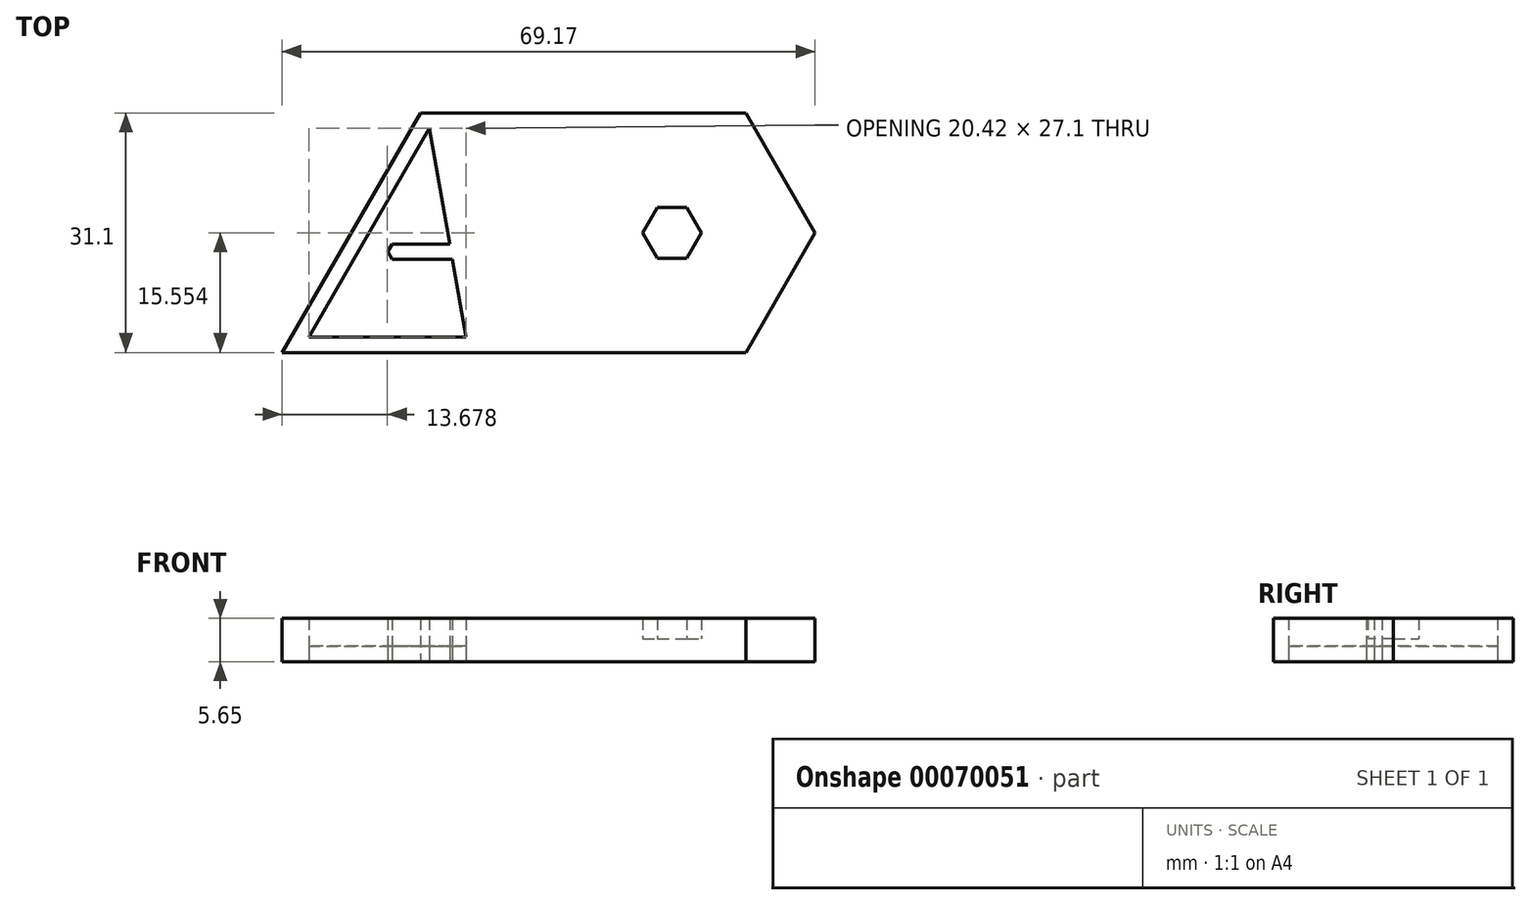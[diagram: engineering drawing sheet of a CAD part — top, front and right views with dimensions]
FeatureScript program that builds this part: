
annotation { "Feature Type Name" : "Feature", "Feature Type Description" : "" }
export const myFeature = defineFeature(function(context is Context, id is Id, definition is map)
    precondition{}
    {
        {
            var Q0;
            Q0=qCreatedBy(makeId("Top.planeOp"),FACE);
            var sketch = newSketch(context, id + "F0", { "sketchPlane" : qUnion([Q0])});
            skLineSegment(sketch, "E0", {"start": v(-58.85, -4.43) * mm, "end": v(-38.43, -4.43) * mm});
            skLineSegment(sketch, "E1", {"start": v(-38.43, -4.43) * mm, "end": v(-43.2, 22.67) * mm});
            skLineSegment(sketch, "E2", {"start": v(-43.2, 22.67) * mm, "end": v(-58.85, -4.43) * mm});
            skLineSegment(sketch, "E3", {"start": v(-40.2, 5.66) * mm, "end": v(-48, 5.66) * mm});
            skLineSegment(sketch, "E4", {"start": v(-38.43, -4.43) * mm, "end": v(-3.28, -4.43) * mm});
            skLineSegment(sketch, "E5", {"start": v(-43.2, 22.67) * mm, "end": v(-3.28, 22.67) * mm});
            skLineSegment(sketch, "E6", {"start": v(-3.28, -4.43) * mm, "end": v(4.54, 9.12) * mm});
            skLineSegment(sketch, "E7", {"start": v(4.54, 9.12) * mm, "end": v(-3.28, 22.67) * mm});
            skPoint(sketch, "E8.endSnap0", {"position": v(-40.82, 9.12) * mm});
            skLineSegment(sketch, "E9.0", {"start": v(-44.36, 24.67) * mm, "end": v(-2.86, 24.67) * mm});
            skLineSegment(sketch, "E9.1", {"start": v(-62.32, -6.43) * mm, "end": v(-38.92, -6.43) * mm});
            skLineSegment(sketch, "E9.2", {"start": v(-38.92, -6.43) * mm, "end": v(-2.13, -6.43) * mm});
            skLineSegment(sketch, "E9.3", {"start": v(-44.36, 24.67) * mm, "end": v(-62.32, -6.43) * mm});
            skLineSegment(sketch, "E9.4", {"start": v(-2.13, -6.43) * mm, "end": v(6.85, 9.12) * mm});
            skLineSegment(sketch, "E10", {"start": v(-48, 7.66) * mm, "end": v(-40.56, 7.66) * mm});
            skLineSegment(sketch, "E11", {"start": v(-41.2, 22.67) * mm, "end": v(-36.43, -4.43) * mm});
            skLineSegment(sketch, "E12", {"start": v(-43.2, 22.67) * mm, "end": v(-41.2, 22.67) * mm});
            skLineSegment(sketch, "E13", {"start": v(-23.52, -4.43) * mm, "end": v(-25.52, -4.43) * mm});
            skLineSegment(sketch, "E14", {"start": v(-33.49, 8.88) * mm, "end": v(-25.52, 8.88) * mm});
            skLineSegment(sketch, "E15", {"start": v(-22.8, 10.88) * mm, "end": v(-33.49, 10.88) * mm});
            skLineSegment(sketch, "E16", {"start": v(-25.6, 14.8) * mm, "end": v(-33.29, 22.67) * mm});
            skLineSegment(sketch, "E17", {"start": v(-48, 5.66) * mm, "end": v(-48.59, 6.66) * mm});
            skLineSegment(sketch, "E18", {"start": v(-48.59, 6.66) * mm, "end": v(-48, 7.66) * mm});
            skLineSegment(sketch, "E19", {"start": v(-33.49, 8.88) * mm, "end": v(-34.07, 9.88) * mm});
            skLineSegment(sketch, "E20", {"start": v(-34.07, 9.88) * mm, "end": v(-33.49, 10.88) * mm});
            skLineSegment(sketch, "E21", {"start": v(-24.17, 16.19) * mm, "end": v(-30.54, 22.67) * mm});
            skLineSegment(sketch, "E22", {"start": v(-25.6, 14.8) * mm, "end": v(-24.48, 15.08) * mm});
            skLineSegment(sketch, "E23", {"start": v(-24.48, 15.08) * mm, "end": v(-24.17, 16.19) * mm});
            skLineSegment(sketch, "E24", {"start": v(-25.52, 8.88) * mm, "end": v(-23.18, -4.43) * mm});
            skLineSegment(sketch, "E25", {"start": v(-22.8, 10.88) * mm, "end": v(-20.1, -4.43) * mm});
            skLineSegment(sketch, "E26", {"start": v(-24.48, 15.08) * mm, "end": v(-20.1, 22.67) * mm});
            skLineSegment(sketch, "E27", {"start": v(-20.1, 22.67) * mm, "end": v(-3.28, 22.67) * mm});
            skLineSegment(sketch, "E28", {"start": v(-20.1, -4.43) * mm, "end": v(-3.28, -4.43) * mm});
            skPoint(sketch, "E29", {"position": v(-11.69, 22.67) * mm});
            skPoint(sketch, "E30", {"position": v(-11.69, 9.12) * mm});
            skCircle(sketch, "E31.cCircle", {"center": v(-11.69, 9.12) * mm, "radius": 3.3 * mm, "construction": true});
            skLineSegment(sketch, "E31.0", {"start": v(-13.6, 12.42) * mm, "end": v(-9.78, 12.42) * mm});
            skLineSegment(sketch, "E31.1", {"start": v(-9.78, 12.42) * mm, "end": v(-7.88, 9.12) * mm});
            skLineSegment(sketch, "E31.2", {"start": v(-7.88, 9.12) * mm, "end": v(-9.78, 5.82) * mm});
            skLineSegment(sketch, "E31.3", {"start": v(-9.78, 5.82) * mm, "end": v(-13.6, 5.82) * mm});
            skLineSegment(sketch, "E31.4", {"start": v(-13.6, 5.82) * mm, "end": v(-15.5, 9.12) * mm});
            skLineSegment(sketch, "E31.5", {"start": v(-15.5, 9.12) * mm, "end": v(-13.6, 12.42) * mm});
            skPoint(sketch, "E31.0.midPoint", {"position": v(-11.69, 12.42) * mm});
            skLineSegment(sketch, "E32.0", {"start": v(6.27, 10.12) * mm, "end": v(-2.13, 24.67) * mm});
            skLineSegment(sketch, "E32.1", {"start": v(-20.1, 24.67) * mm, "end": v(-2.13, 24.67) * mm});
            skLineSegment(sketch, "E33", {"start": v(6.27, 10.12) * mm, "end": v(6.85, 9.12) * mm});
            skSolve(sketch);
        }
        {
            var Q0;
            {var subQ3=sQuery(id+"F0.wireOp",EDGE,"E0");Q0=makeQuery(id+"F0.imprint","IMPRINT",FACE,{"disambiguationData":[TD([[makeQuery(id+"F0.imprint","IMPRINT",EDGE,{"derivedFrom":subQ3}),1.0]])]});}
            var Q1;
            {var subQ9=sQuery(id+"F0.wireOp",EDGE,"E6");Q1=makeQuery(id+"F0.imprint","IMPRINT",FACE,{"disambiguationData":[TD([[makeQuery(id+"F0.imprint","IMPRINT",EDGE,{"derivedFrom":subQ9}),1.0]])]});}
            extrude(context, id + "F1", {"entities" : qUnion([Q0, Q1]), "depth" : 2 * mm});
        }
        {
            var Q0;
            {var subQ3=sQuery(id+"F0.wireOp",EDGE,"E11");Q0=makeQuery(id+"F0.imprint","IMPRINT",FACE,{"disambiguationData":[TD([[makeQuery(id+"F0.imprint","IMPRINT",EDGE,{"derivedFrom":subQ3}),-1.0]])]});}
            var Q1;
            {var subQ0=sQuery(id+"F0.wireOp",EDGE,"E3");Q1=makeQuery(id+"F0.imprint","IMPRINT",FACE,{"disambiguationData":[TD([[makeQuery(id+"F0.imprint","IMPRINT",EDGE,{"derivedFrom":subQ0}),-1.0]])]});}
            var Q2;
            Q2=makeQuery(id+"F0.imprint","IMPRINT",FACE,{"disambiguationData":[TD([[makeQuery(id+"F0.imprint","IMPRINT",EDGE,{"derivedFrom":sQuery(id+"F0.wireOp",EDGE,"E14")}),1.0]])]});
            var Q3;
            {var subQ0=sQuery(id+"F0.wireOp",EDGE,"E16");Q3=makeQuery(id+"F0.imprint","IMPRINT",FACE,{"disambiguationData":[TD([[makeQuery(id+"F0.imprint","IMPRINT",EDGE,{"derivedFrom":subQ0}),-1.0]])]});}
            var Q4;
            {var subQ0=sQuery(id+"F0.wireOp",EDGE,"E21");Q4=makeQuery(id+"F0.imprint","IMPRINT",FACE,{"disambiguationData":[TD([[makeQuery(id+"F0.imprint","IMPRINT",EDGE,{"derivedFrom":subQ0}),-1.0]])]});}
            var Q5;
            {var subQ7=sQuery(id+"F0.wireOp",EDGE,"E0");Q5=makeQuery(id+"F0.imprint","IMPRINT",FACE,{"disambiguationData":[TD([[makeQuery(id+"F0.imprint","IMPRINT",EDGE,{"derivedFrom":subQ7}),-1.0]])]});}
            var Q6;
            Q6=makeQuery(id+"F0.imprint","IMPRINT",FACE,{"disambiguationData":[TD([[makeQuery(id+"F0.imprint","IMPRINT",EDGE,{"derivedFrom":sQuery(id+"F0.wireOp",EDGE,"E6")}),1.0]])]});
            extrude(context, id + "F2", {"entities" : qUnion([Q0, Q1, Q2, Q3, Q4, Q5, Q6]), "depth" : 5.65 * mm});
        }
        {
            var Q0;
            Q0=makeQuery(id+"F0.imprint","IMPRINT",FACE,{"disambiguationData":[TD([[makeQuery(id+"F0.imprint","IMPRINT",EDGE,{"derivedFrom":sQuery(id+"F0.wireOp",EDGE,"E31.0")}),-1.0]])]});
            extrude(context, id + "F3", {"entities" : qUnion([Q0]), "operationType" : NewBodyOperationType.ADD, "depth" : 3 * mm});
        }
    });
